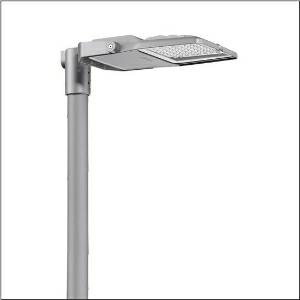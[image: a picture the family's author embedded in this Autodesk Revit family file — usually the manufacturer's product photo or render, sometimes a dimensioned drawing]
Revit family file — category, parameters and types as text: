
# Revit family: floodlight_fl_21_iq_mini___pl61_5xa7771c2c3a_2691
name_source: partatom
category: Lighting Fixtures
units: mm (PartAtom-declared; Revit-internal decimal feet)

## family parameters
Cut with Voids When Loaded = No
Host = Face
Light Source = No
Part Type = Normal
Room Calculation Point = No
Round Connector Dimension = Use Diameter
Shared = No

## types (1)
- --- (1 x LED, 11980 lm, 87.2 W, 3000K)
    Apparent Load = 87 VA
    CIE Flux Codes = 33 65 98 100 100
    Color Rendering = 70
    Color Temperature = 3000K
    Default Elevation = 1800 mm
    Description = Floodlight FL 21 iQ mini, floodlight, primary light control with lens, of PMMA, primary optical cover: protective disc, of toughened safety glass, transparent, light distribution: PL61, light emission: direct distribution, installation type: surface-mounted, lamps: LED, High Power LED, rated values: 11.980lm | 87,2W | 137,4lm/W (begin service life); end service life: 11.980lm | 92,1W; at 50% lumin. flux: 5.990lm | 40,1W | 149,4lm/W, colour temperature: 3000K, colour rendering: CRI > 70, light colour: 730, light setting 1 begin service life: 100% | 11.980lm | 87,2W | 137,4lm/W | 3.000K, light setting 1 end service life: 92,1W, further light settings possible, control: Auto-Match, Temp-Guard, Lumen-Switch, Night-Set, Smart-Wire, Light-Fading, Desk-Remote (wireless, voltage-free reading and setting of iQ features in the workshop via application-optimized NFC function/RFID function), optimised constant luminous flux control (CLO 2.0), pre-setting: linear dimming characteristic, with terminal, 6-pole, mains connection: 220..240V, AC, 50/60Hz, luminaire housing, of diecast aluminium, powder-coated, SITECO metallic grey (DB 702S), corrosivity category C5 mid according to DIN EN ISO 12944suitable for swimming poolschlorine-resistant, sealing non-destructively replaceable, please order mast flange separately, mast bracket, of steel, galvanised, powder-coated, SITECO metallic grey (DB 702S), protection rating (complete): IP66, insulation class (complete): insulation class II (safety insulation), certification: CE, ENEC, VDE, protection symbol: D, impact resistance: IK08, permissible operating ambient temperature: -40..+40°C, permissible operating ambient temperature for outdoor applications: -40..+50°C, standard: DIN EN 12944, LABS conformity tested according to VDMA 24364:2018-05, packaging unit: 1 piece

Light Distribution: PL61
    Height = 70 mm
    Lamp = 1 x LED
    Lamp Light Flux = 11980 lm
    Lamp Power = 87.2 W
    Lamp count = 1
    Length = 485 mm
    Luminous efficacy = 137 lm/W
    Manufacturer = Siteco
    ModVariant = No
    Model = 5XA7771C2C3A
    Number of Poles = 1
    OnlyDefault = Yes
    Power Factor = 1
    Product Name = Floodlight FL 21 iQ mini | PL61
    Product group = floodlight | pylon annexe
    ProductGroupID = 6201
    Protection Class = Protection class II
    Protection Degree = IP 66
    RLX_Detail_Level = 1
    RLX_Emergency_Light_Flux = 0 lm
    RLX_Emergency_Type = 0
    RLX_Emergency_Type_DB = No
    RlxData = <blob elided: 101705 chars, md5=1050cbfa>
    Socket = socket
    Standby Power = 0 W
    System Light Flux = 11980 lm
    System Power = 87 W
    Type Comments = factory setting: luminous flux: 100 % | dim-lin: 254 | 456 mA
    Type Image = l_1007125.jpg
    URL = http://relux.com
    VarID = @adj_172781
    Voltage = 0 V
    Weight = 0.00 kg
    Width = 337 mm

## geometry (parser evidence)
native form markers: Blend x4, Sweep x12
no freeform markers — native parametric forms only
